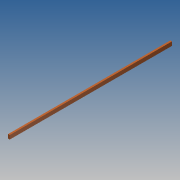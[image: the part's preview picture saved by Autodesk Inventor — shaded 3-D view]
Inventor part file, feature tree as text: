
AUTODESK INVENTOR PART (.ipt)
format: ipt  version: 2013 (Build 170138000, 138)  size: 68,608 bytes
history: native  units: in
note: dims shown in document units (in); Inventor stores cm internally (conversion verified against a paired STEP export)
features: extrude x1, sketch x1
ambient origin geometry x8: Origin, YZ Plane, XZ Plane, XY Plane, X Axis, Y Axis, Z Axis, Center Point
bodies: Solid1 (feature_tree)
feature tree (2):
  extrude  "Extrusion1"  Depth=3.5in
  sketch  "Sketch2"  dims[d0=1.5in d1=3.5in d2=145.5in d3=0.0in]
